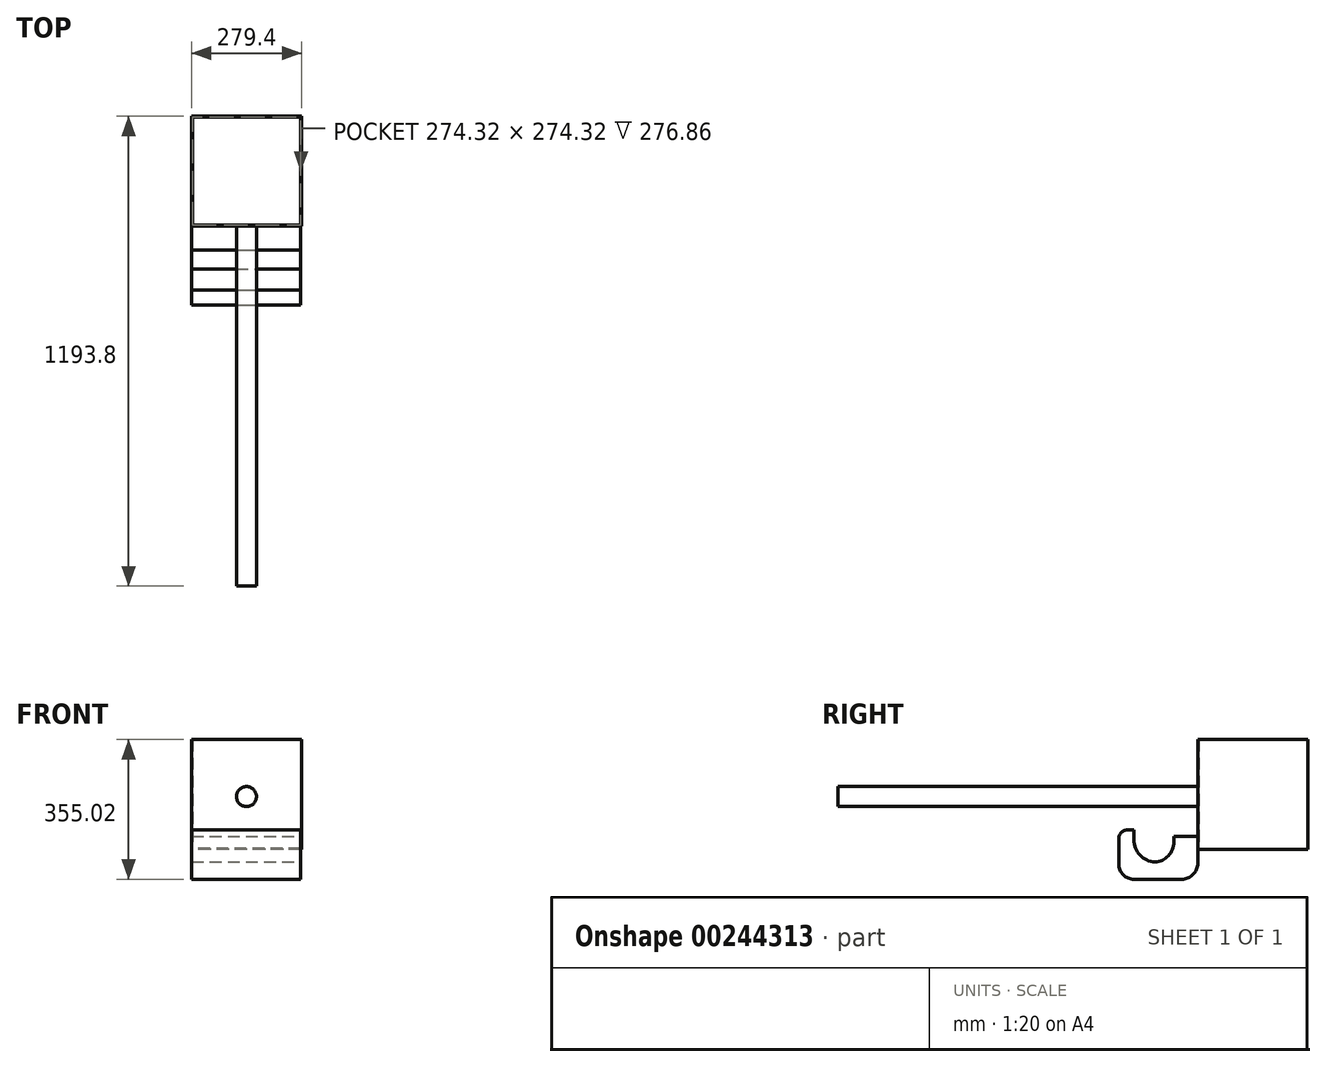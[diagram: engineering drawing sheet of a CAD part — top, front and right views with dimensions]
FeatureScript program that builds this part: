
annotation { "Feature Type Name" : "Feature", "Feature Type Description" : "" }
export const myFeature = defineFeature(function(context is Context, id is Id, definition is map)
    precondition{}
    {
        {
            var Q0;
            Q0=qCreatedBy(makeId("Right.planeOp"),FACE);
            var sketch = newSketch(context, id + "F0", { "sketchPlane" : qUnion([Q0])});
            skLineSegment(sketch, "E0.bottom", {"start": v(-147.83, 144.93) * mm, "end": v(131.57, 144.93) * mm});
            skLineSegment(sketch, "E0.top", {"start": v(-147.83, -134.47) * mm, "end": v(131.57, -134.47) * mm});
            skLineSegment(sketch, "E0.left", {"start": v(-147.83, 144.93) * mm, "end": v(-147.83, -134.47) * mm});
            skLineSegment(sketch, "E0.right", {"start": v(131.57, 144.93) * mm, "end": v(131.57, -134.47) * mm});
            skSolve(sketch);
        }
        {
            var Q0;
            Q0 = qSketchRegion(id + "F0", true);
            extrude(context, id + "F1", {"entities" : qUnion([Q0]), "depth" : 279.4 * mm});
        }
        {
            var Q0;
            Q0=makeQuery(id+"F1.opExtrude","SWEPT_FACE",FACE,{"disambiguationData":[OSD([sQuery(id+"F0.wireOp",EDGE,"E0.bottom")])]});
            shell(context, id + "F2", {"entities" : qUnion([Q0]), "thickness" : 2.54 * mm});
        }
        {
            var Q0;
            Q0=makeQuery(id+"F1.opExtrude","SWEPT_FACE",FACE,{"disambiguationData":[OSD([sQuery(id+"F0.wireOp",EDGE,"E0.left")])]});
            var sketch = newSketch(context, id + "F3", { "sketchPlane" : qUnion([Q0])});
            skCircle(sketch, "E1", {"center": v(139.3, 0) * mm, "radius": 25.4 * mm});
            skSolve(sketch);
        }
        {
            var Q0;
            Q0=makeQuery(id+"F3.imprint","IMPRINT",FACE,{"disambiguationData":[TD([[makeQuery(id+"F3.imprint","IMPRINT",EDGE,{"derivedFrom":sQuery(id+"F3.wireOp",EDGE,"E1")}),1.0]])]});
            extrude(context, id + "F4", {"entities" : qUnion([Q0]), "operationType" : NewBodyOperationType.ADD, "depth" : 914.4 * mm});
        }
        {
            var Q0;
            Q0=makeQuery(id+"F1.opExtrude","CAP_FACE",FACE,{"disambiguationData":[OSD([sQuery(id+"F0.wireOp",EDGE,"E0.bottom"),sQuery(id+"F0.wireOp",EDGE,"E0.top"),sQuery(id+"F0.wireOp",EDGE,"E0.left"),sQuery(id+"F0.wireOp",EDGE,"E0.right")])],"isStart":false});
            var sketch = newSketch(context, id + "F5", { "sketchPlane" : qUnion([Q0])});
            skLineSegment(sketch, "E2", {"start": v(-147.83, -101.43) * mm, "end": v(-208.7, -101.43) * mm});
            skLineSegment(sketch, "E3", {"start": v(-208.7, -101.43) * mm, "end": v(-208.7, -115.56) * mm});
            skLineSegment(sketch, "E4", {"start": v(-253.5, -166.36) * mm, "end": v(-259.5, -166.36) * mm});
            skLineSegment(sketch, "E5", {"start": v(-310.3, -109.56) * mm, "end": v(-310.3, -84.2) * mm});
            skLineSegment(sketch, "E6", {"start": v(-310.3, -84.2) * mm, "end": v(-325.19, -84.2) * mm});
            skLineSegment(sketch, "E7", {"start": v(-348.73, -107.75) * mm, "end": v(-348.73, -171.14) * mm});
            skLineSegment(sketch, "E8", {"start": v(-309.78, -210.09) * mm, "end": v(-188.7, -210.09) * mm});
            skLineSegment(sketch, "E9", {"start": v(-147.83, -169.2) * mm, "end": v(-147.83, -101.43) * mm});
            skPoint(sketch, "E10.visualSharp", {"position": v(-310.3, -166.36) * mm});
            skArc(sketch, "E10.filletArc", {"start": v(-310.3, -109.56) * mm, "mid": v(-293.66, -149.72) * mm, "end": v(-253.5, -166.36) * mm});
            skPoint(sketch, "E11.visualSharp", {"position": v(-208.7, -166.36) * mm});
            skArc(sketch, "E11.filletArc", {"start": v(-259.5, -166.36) * mm, "mid": v(-223.58, -151.48) * mm, "end": v(-208.7, -115.56) * mm});
            skPoint(sketch, "E12.visualSharp", {"position": v(-348.73, -210.09) * mm});
            skArc(sketch, "E12.filletArc", {"start": v(-348.73, -171.14) * mm, "mid": v(-337.32, -198.68) * mm, "end": v(-309.78, -210.09) * mm});
            skPoint(sketch, "E13.visualSharp", {"position": v(-147.83, -210.09) * mm});
            skArc(sketch, "E13.filletArc", {"start": v(-188.7, -210.09) * mm, "mid": v(-159.8, -198.12) * mm, "end": v(-147.83, -169.2) * mm});
            skPoint(sketch, "E14.visualSharp", {"position": v(-348.73, -84.2) * mm});
            skArc(sketch, "E14.filletArc", {"start": v(-325.19, -84.2) * mm, "mid": v(-341.83, -91.1) * mm, "end": v(-348.73, -107.75) * mm});
            skSolve(sketch);
        }
        {
            var Q0;
            Q0 = qSketchRegion(id + "F5", true);
            extrude(context, id + "F6", {"entities" : qUnion([Q0]), "oppositeDirection" : true, "depth" : 279.4 * mm, "hasSecondDirection" : true, "secondDirectionOppositeDirection" : true, "secondDirectionDepth" : 2.54 * mm});
        }
    });
